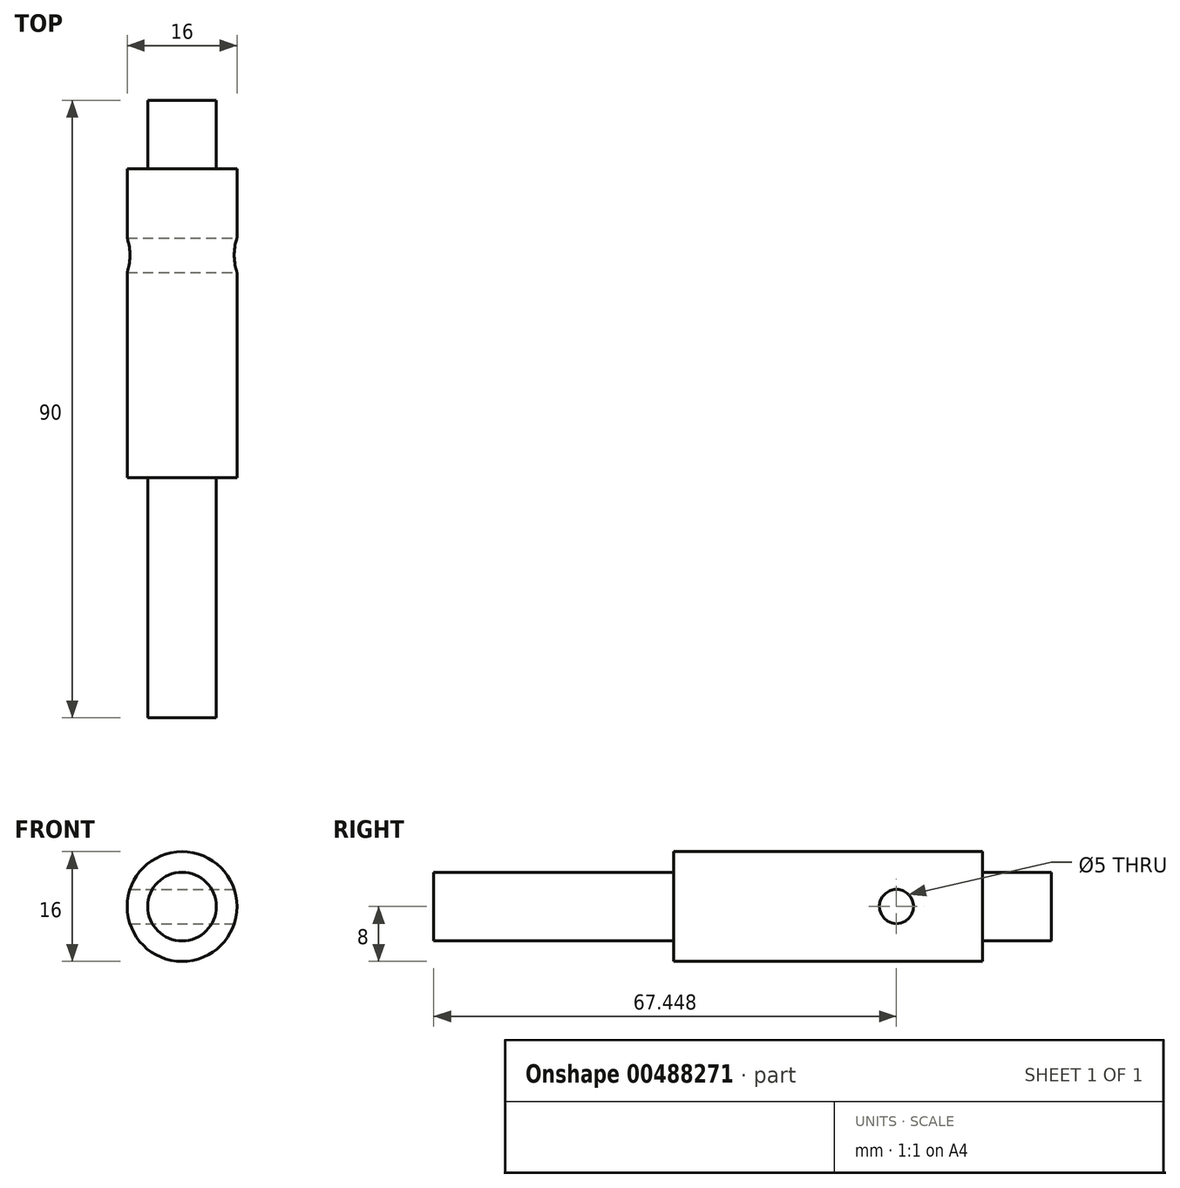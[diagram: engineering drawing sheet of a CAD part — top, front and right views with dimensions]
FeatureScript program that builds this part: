
annotation { "Feature Type Name" : "Feature", "Feature Type Description" : "" }
export const myFeature = defineFeature(function(context is Context, id is Id, definition is map)
    precondition{}
    {
        {
            var Q0;
            Q0=qCreatedBy(makeId("Top.planeOp"),FACE);
            var sketch = newSketch(context, id + "F0", { "sketchPlane" : qUnion([Q0])});
            skLineSegment(sketch, "E0", {"start": v(0, 30.3) * mm, "end": v(0, -59.7) * mm});
            skLineSegment(sketch, "E1", {"start": v(0, 30.3) * mm, "end": v(-5, 30.3) * mm});
            skLineSegment(sketch, "E2", {"start": v(-5, 30.3) * mm, "end": v(-5, 20.3) * mm});
            skLineSegment(sketch, "E3", {"start": v(0, -59.7) * mm, "end": v(-5, -59.7) * mm});
            skLineSegment(sketch, "E4", {"start": v(-5, -59.7) * mm, "end": v(-5, -24.7) * mm});
            skLineSegment(sketch, "E5", {"start": v(-5, 20.3) * mm, "end": v(-8, 20.3) * mm});
            skLineSegment(sketch, "E6", {"start": v(-8, 20.3) * mm, "end": v(-8, -24.7) * mm});
            skLineSegment(sketch, "E7", {"start": v(-8, -24.7) * mm, "end": v(-5, -24.7) * mm});
            skSolve(sketch);
        }
        {
            var Q0;
            Q0 = qSketchRegion(id + "F0", true);
            var Q1;
            Q1=sQuery(id+"F0.wireOp",EDGE,"E0");
            revolve(context, id + "F1", {"entities" : qUnion([Q0]), "axis" : qUnion([Q1]), "revolveType" : RevolveType.FULL});
        }
        {
            var Q0;
            Q0=qCreatedBy(makeId("Right.planeOp"),FACE);
            cPlane(context, id + "F2", {"entities" : qUnion([Q0]), "cplaneType" : CPlaneType.OFFSET, "offset" : 25 * mm, "width" : 150 * mm, "height" : 150 * mm});
        }
        {
            var Q0;
            Q0=qCreatedBy(id+"F2.planeOp",FACE);
            var sketch = newSketch(context, id + "F3", { "sketchPlane" : qUnion([Q0])});
            skCircle(sketch, "E8", {"center": v(7.75, 0) * mm, "radius": 2.5 * mm});
            skSolve(sketch);
        }
        {
            var Q0;
            Q0 = qSketchRegion(id + "F3", true);
            extrude(context, id + "F4", {"entities" : qUnion([Q0]), "operationType" : NewBodyOperationType.REMOVE, "oppositeDirection" : true, "depth" : 45 * mm});
        }
    });
